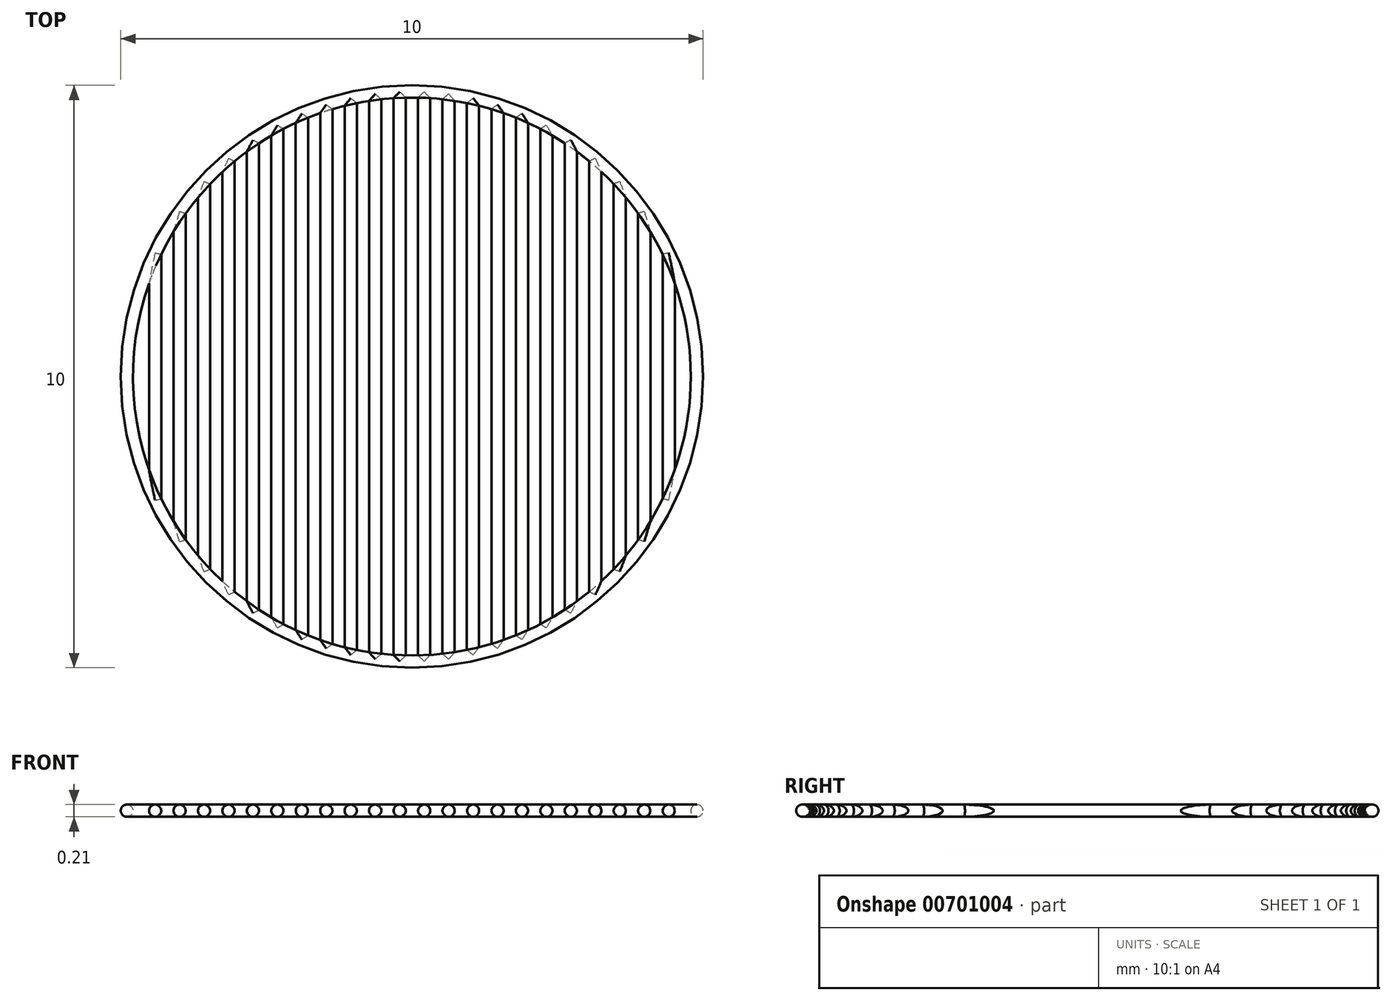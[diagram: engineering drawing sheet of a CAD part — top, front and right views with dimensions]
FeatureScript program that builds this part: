
annotation { "Feature Type Name" : "Feature", "Feature Type Description" : "" }
export const myFeature = defineFeature(function(context is Context, id is Id, definition is map)
    precondition{}
    {
        {
            assignVariable(context, id + "F0", {"name" : "d", "anyValue" : 0.2 * mm});
        }
        {
            var Q0;
            Q0=qCreatedBy(makeId("Top.planeOp"),FACE);
            cPlane(context, id + "F1", {"entities" : qUnion([Q0]), "cplaneType" : CPlaneType.OFFSET, "offset" : getVariable(context, 'd') / 2, "width" : 150 * mm, "height" : 150 * mm});
        }
        {
            var Q0;
            Q0=qCreatedBy(id+"F1.planeOp",FACE);
            var sketch = newSketch(context, id + "F2", { "sketchPlane" : qUnion([Q0])});
            skLineSegment(sketch, "E0.bottom", {"start": v(5, 5) * mm, "end": v(-5, 5) * mm, "construction": true});
            skLineSegment(sketch, "E0.top", {"start": v(5, -5) * mm, "end": v(-5, -5) * mm, "construction": true});
            skLineSegment(sketch, "E0.left", {"start": v(5, 5) * mm, "end": v(5, -5) * mm, "construction": true});
            skLineSegment(sketch, "E0.right", {"start": v(-5, 5) * mm, "end": v(-5, -5) * mm, "construction": true});
            skPoint(sketch, "E0.middle", {"position": v(0, 0) * mm});
            skCircle(sketch, "E1", {"center": v(0, 0) * mm, "radius": 4.8 * mm, "construction": true});
            skLineSegment(sketch, "E2", {"start": v(-5, 5) * mm, "end": v(-4.4, 5) * mm, "construction": true});
            skLineSegment(sketch, "E3", {"start": v(-4.4, 5) * mm, "end": v(-4.4, -5) * mm, "construction": true});
            skLineSegment(sketch, "E4", {"start": v(-4.4, -5) * mm, "end": v(-5, -5) * mm, "construction": true});
            skCircle(sketch, "E5", {"center": v(0, 0) * mm, "radius": 4.9 * mm});
            skLineSegment(sketch, "E6", {"start": v(-4.4, 5) * mm, "end": v(-3.99, 5) * mm, "construction": true});
            skLineSegment(sketch, "E7", {"start": v(-3.99, 5) * mm, "end": v(-3.99, -5) * mm, "construction": true});
            skLineSegment(sketch, "E8", {"start": v(-3.99, -5) * mm, "end": v(-4.4, -5) * mm, "construction": true});
            skLineSegment(sketch, "E9.1.0.0", {"start": v(-3.99, 5) * mm, "end": v(-3.57, 5) * mm, "construction": true});
            skLineSegment(sketch, "E9.1.0.1", {"start": v(-3.57, 5) * mm, "end": v(-3.57, -5) * mm, "construction": true});
            skLineSegment(sketch, "E9.1.0.2", {"start": v(-3.57, -5) * mm, "end": v(-3.99, -5) * mm, "construction": true});
            skLineSegment(sketch, "E9.2.0.0", {"start": v(-3.57, 5) * mm, "end": v(-3.15, 5) * mm, "construction": true});
            skLineSegment(sketch, "E9.2.0.1", {"start": v(-3.15, 5) * mm, "end": v(-3.15, -5) * mm, "construction": true});
            skLineSegment(sketch, "E9.2.0.2", {"start": v(-3.15, -5) * mm, "end": v(-3.57, -5) * mm, "construction": true});
            skLineSegment(sketch, "E9.3.0.0", {"start": v(-3.15, 5) * mm, "end": v(-2.73, 5) * mm, "construction": true});
            skLineSegment(sketch, "E9.3.0.1", {"start": v(-2.73, 5) * mm, "end": v(-2.73, -5) * mm, "construction": true});
            skLineSegment(sketch, "E9.3.0.2", {"start": v(-2.73, -5) * mm, "end": v(-3.15, -5) * mm, "construction": true});
            skLineSegment(sketch, "E9.4.0.0", {"start": v(-2.73, 5) * mm, "end": v(-2.3, 5) * mm, "construction": true});
            skLineSegment(sketch, "E9.4.0.1", {"start": v(-2.3, 5) * mm, "end": v(-2.3, -5) * mm, "construction": true});
            skLineSegment(sketch, "E9.4.0.2", {"start": v(-2.3, -5) * mm, "end": v(-2.73, -5) * mm, "construction": true});
            skLineSegment(sketch, "E9.5.0.0", {"start": v(-2.3, 5) * mm, "end": v(-1.89, 5) * mm, "construction": true});
            skLineSegment(sketch, "E9.5.0.1", {"start": v(-1.89, 5) * mm, "end": v(-1.89, -5) * mm, "construction": true});
            skLineSegment(sketch, "E9.5.0.2", {"start": v(-1.89, -5) * mm, "end": v(-2.3, -5) * mm, "construction": true});
            skLineSegment(sketch, "E9.6.0.0", {"start": v(-1.89, 5) * mm, "end": v(-1.47, 5) * mm, "construction": true});
            skLineSegment(sketch, "E9.6.0.1", {"start": v(-1.47, 5) * mm, "end": v(-1.47, -5) * mm, "construction": true});
            skLineSegment(sketch, "E9.6.0.2", {"start": v(-1.47, -5) * mm, "end": v(-1.89, -5) * mm, "construction": true});
            skLineSegment(sketch, "E9.7.0.0", {"start": v(-1.47, 5) * mm, "end": v(-1.05, 5) * mm, "construction": true});
            skLineSegment(sketch, "E9.7.0.1", {"start": v(-1.05, 5) * mm, "end": v(-1.05, -5) * mm, "construction": true});
            skLineSegment(sketch, "E9.7.0.2", {"start": v(-1.05, -5) * mm, "end": v(-1.47, -5) * mm, "construction": true});
            skLineSegment(sketch, "E9.8.0.0", {"start": v(-1.05, 5) * mm, "end": v(-0.63, 5) * mm, "construction": true});
            skLineSegment(sketch, "E9.8.0.1", {"start": v(-0.63, 5) * mm, "end": v(-0.63, -5) * mm, "construction": true});
            skLineSegment(sketch, "E9.8.0.2", {"start": v(-0.63, -5) * mm, "end": v(-1.05, -5) * mm, "construction": true});
            skLineSegment(sketch, "E9.9.0.0", {"start": v(-0.63, 5) * mm, "end": v(-0.2, 5) * mm, "construction": true});
            skLineSegment(sketch, "E9.9.0.1", {"start": v(-0.2, 5) * mm, "end": v(-0.2, -5) * mm, "construction": true});
            skLineSegment(sketch, "E9.9.0.2", {"start": v(-0.2, -5) * mm, "end": v(-0.63, -5) * mm, "construction": true});
            skLineSegment(sketch, "E9.10.0.0", {"start": v(-0.2, 5) * mm, "end": v(0.21, 5) * mm, "construction": true});
            skLineSegment(sketch, "E9.10.0.1", {"start": v(0.21, 5) * mm, "end": v(0.21, -5) * mm, "construction": true});
            skLineSegment(sketch, "E9.10.0.2", {"start": v(0.21, -5) * mm, "end": v(-0.2, -5) * mm, "construction": true});
            skLineSegment(sketch, "E10.0.11.0", {"start": v(0.21, 5) * mm, "end": v(0.63, 5) * mm, "construction": true});
            skLineSegment(sketch, "E10.3.11.0", {"start": v(0.63, 5) * mm, "end": v(0.63, -5) * mm, "construction": true});
            skLineSegment(sketch, "E10.6.11.0", {"start": v(0.63, -5) * mm, "end": v(0.21, -5) * mm, "construction": true});
            skLineSegment(sketch, "E10.0.12.0", {"start": v(0.63, 5) * mm, "end": v(1.05, 5) * mm, "construction": true});
            skLineSegment(sketch, "E10.3.12.0", {"start": v(1.05, 5) * mm, "end": v(1.05, -5) * mm, "construction": true});
            skLineSegment(sketch, "E10.6.12.0", {"start": v(1.05, -5) * mm, "end": v(0.63, -5) * mm, "construction": true});
            skLineSegment(sketch, "E11.0.13.0", {"start": v(1.05, 5) * mm, "end": v(1.47, 5) * mm, "construction": true});
            skLineSegment(sketch, "E11.3.13.0", {"start": v(1.47, 5) * mm, "end": v(1.47, -5) * mm, "construction": true});
            skLineSegment(sketch, "E11.6.13.0", {"start": v(1.47, -5) * mm, "end": v(1.05, -5) * mm, "construction": true});
            skLineSegment(sketch, "E11.0.14.0", {"start": v(1.47, 5) * mm, "end": v(1.9, 5) * mm, "construction": true});
            skLineSegment(sketch, "E11.3.14.0", {"start": v(1.9, 5) * mm, "end": v(1.9, -5) * mm, "construction": true});
            skLineSegment(sketch, "E11.6.14.0", {"start": v(1.9, -5) * mm, "end": v(1.47, -5) * mm, "construction": true});
            skLineSegment(sketch, "E11.0.15.0", {"start": v(1.9, 5) * mm, "end": v(2.31, 5) * mm, "construction": true});
            skLineSegment(sketch, "E11.3.15.0", {"start": v(2.31, 5) * mm, "end": v(2.31, -5) * mm, "construction": true});
            skLineSegment(sketch, "E11.6.15.0", {"start": v(2.31, -5) * mm, "end": v(1.9, -5) * mm, "construction": true});
            skLineSegment(sketch, "E11.0.16.0", {"start": v(2.31, 5) * mm, "end": v(2.73, 5) * mm, "construction": true});
            skLineSegment(sketch, "E11.3.16.0", {"start": v(2.73, 5) * mm, "end": v(2.73, -5) * mm, "construction": true});
            skLineSegment(sketch, "E11.6.16.0", {"start": v(2.73, -5) * mm, "end": v(2.31, -5) * mm, "construction": true});
            skLineSegment(sketch, "E11.0.17.0", {"start": v(2.73, 5) * mm, "end": v(3.15, 5) * mm, "construction": true});
            skLineSegment(sketch, "E11.3.17.0", {"start": v(3.15, 5) * mm, "end": v(3.15, -5) * mm, "construction": true});
            skLineSegment(sketch, "E11.6.17.0", {"start": v(3.15, -5) * mm, "end": v(2.73, -5) * mm, "construction": true});
            skLineSegment(sketch, "E11.0.18.0", {"start": v(3.15, 5) * mm, "end": v(3.57, 5) * mm, "construction": true});
            skLineSegment(sketch, "E11.3.18.0", {"start": v(3.57, 5) * mm, "end": v(3.57, -5) * mm, "construction": true});
            skLineSegment(sketch, "E11.6.18.0", {"start": v(3.57, -5) * mm, "end": v(3.15, -5) * mm, "construction": true});
            skLineSegment(sketch, "E11.0.19.0", {"start": v(3.57, 5) * mm, "end": v(4, 5) * mm, "construction": true});
            skLineSegment(sketch, "E11.3.19.0", {"start": v(4, 5) * mm, "end": v(4, -5) * mm, "construction": true});
            skLineSegment(sketch, "E11.6.19.0", {"start": v(4, -5) * mm, "end": v(3.57, -5) * mm, "construction": true});
            skLineSegment(sketch, "E12.0.20.0", {"start": v(4, 5) * mm, "end": v(4.4, 5) * mm, "construction": true});
            skLineSegment(sketch, "E12.3.20.0", {"start": v(4.4, 5) * mm, "end": v(4.4, -5) * mm, "construction": true});
            skLineSegment(sketch, "E12.6.20.0", {"start": v(4.41, -5) * mm, "end": v(4, -5) * mm, "construction": true});
            skLineSegment(sketch, "E13", {"start": v(4.4, 5) * mm, "end": v(5, 5) * mm, "construction": true});
            skLineSegment(sketch, "E14", {"start": v(4.41, -5) * mm, "end": v(5, -5) * mm, "construction": true});
            skPoint(sketch, "E15", {"position": v(-4.4, 2.12) * mm});
            skPoint(sketch, "E16", {"position": v(-4.4, -2.12) * mm});
            skSolve(sketch);
        }
        {
            var Q0;
            Q0=qCreatedBy(makeId("Front.planeOp"),FACE);
            var sketch = newSketch(context, id + "F3", { "sketchPlane" : qUnion([Q0])});
            skCircle(sketch, "E17", {"center": v(-4.9, 0.1) * mm, "radius": 0.1 * mm});
            skSolve(sketch);
        }
        {
            var Q0;
            Q0=qCreatedBy(makeId("Front.planeOp"),FACE);
            var sketch = newSketch(context, id + "F4", { "sketchPlane" : qUnion([Q0])});
            skCircle(sketch, "E18", {"center": v(-4.4, 0.1) * mm, "radius": 0.1 * mm});
            skCircle(sketch, "E19", {"center": v(-3.99, 0.1) * mm, "radius": 0.1 * mm});
            skCircle(sketch, "E20", {"center": v(-3.57, 0.1) * mm, "radius": 0.1 * mm});
            skCircle(sketch, "E21", {"center": v(-3.15, 0.1) * mm, "radius": 0.1 * mm});
            skCircle(sketch, "E22", {"center": v(-2.73, 0.1) * mm, "radius": 0.1 * mm});
            skCircle(sketch, "E23", {"center": v(-2.3, 0.1) * mm, "radius": 0.1 * mm});
            skCircle(sketch, "E24", {"center": v(-1.47, 0.1) * mm, "radius": 0.1 * mm});
            skCircle(sketch, "E25", {"center": v(-1.05, 0.1) * mm, "radius": 0.1 * mm});
            skCircle(sketch, "E26", {"center": v(-0.63, 0.1) * mm, "radius": 0.1 * mm});
            skCircle(sketch, "E27", {"center": v(-0.2, 0.1) * mm, "radius": 0.1 * mm});
            skCircle(sketch, "E28", {"center": v(0.21, 0.1) * mm, "radius": 0.1 * mm});
            skCircle(sketch, "E29", {"center": v(-1.89, 0.1) * mm, "radius": 0.1 * mm});
            skCircle(sketch, "E30", {"center": v(0.63, 0.1) * mm, "radius": 0.1 * mm});
            skCircle(sketch, "E31", {"center": v(1.05, 0.1) * mm, "radius": 0.1 * mm});
            skCircle(sketch, "E32", {"center": v(1.47, 0.1) * mm, "radius": 0.1 * mm});
            skCircle(sketch, "E33", {"center": v(1.9, 0.1) * mm, "radius": 0.1 * mm});
            skCircle(sketch, "E34", {"center": v(2.31, 0.1) * mm, "radius": 0.1 * mm});
            skCircle(sketch, "E35", {"center": v(2.73, 0.1) * mm, "radius": 0.1 * mm});
            skCircle(sketch, "E36", {"center": v(3.15, 0.1) * mm, "radius": 0.1 * mm});
            skCircle(sketch, "E37", {"center": v(3.57, 0.1) * mm, "radius": 0.1 * mm});
            skCircle(sketch, "E38", {"center": v(4, 0.1) * mm, "radius": 0.1 * mm});
            skCircle(sketch, "E39", {"center": v(4.4, 0.1) * mm, "radius": 0.1 * mm});
            skSolve(sketch);
        }
        {
            var Q0;
            Q0=makeQuery(id+"F3.imprint","IMPRINT",FACE,{"disambiguationData":[TD([[makeQuery(id+"F3.imprint","IMPRINT",EDGE,{"derivedFrom":sQuery(id+"F3.wireOp",EDGE,"E17")}),1.0]])]});
            var Q1;
            Q1=sQuery(id+"F2.wireOp",EDGE,"E5");
            sweep(context, id + "F5", {"profiles" : qUnion([Q0]), "path" : qUnion([Q1])});
        }
        {
            var Q0;
            Q0=qSketchRegion(id+"F4",true);
            extrude(context, id + "F6", {"entities" : qUnion([Q0]), "endBound" : BoundingType.UP_TO_NEXT, "depth" : 25 * mm, "offsetDistance" : 25 * mm, "hasSecondDirection" : true, "secondDirectionBound" : SecondDirectionBoundingType.UP_TO_NEXT, "secondDirectionOppositeDirection" : true, "secondDirectionDepth" : 25 * mm});
        }
    });
